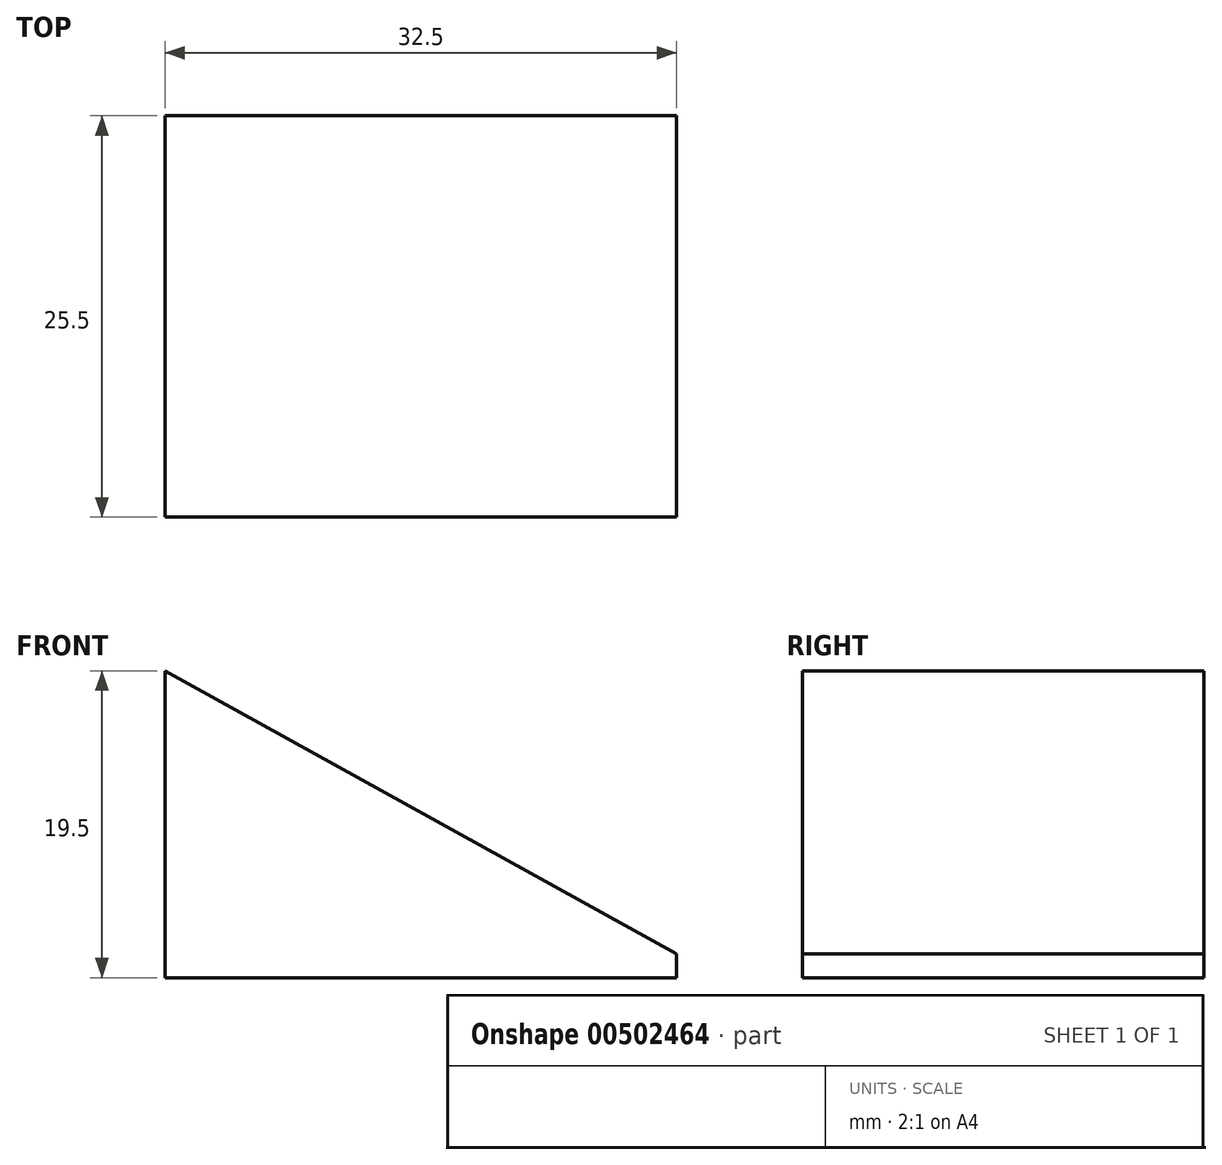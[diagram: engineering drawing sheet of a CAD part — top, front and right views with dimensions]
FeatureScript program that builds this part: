
annotation { "Feature Type Name" : "Feature", "Feature Type Description" : "" }
export const myFeature = defineFeature(function(context is Context, id is Id, definition is map)
    precondition{}
    {
        {
            var Q0;
            Q0=qCreatedBy(makeId("Top.planeOp"),FACE);
            var sketch = newSketch(context, id + "F0", { "sketchPlane" : qUnion([Q0])});
            skLineSegment(sketch, "E0.bottom", {"start": v(16.25, 12.75) * mm, "end": v(-16.25, 12.75) * mm});
            skLineSegment(sketch, "E0.top", {"start": v(16.25, -12.75) * mm, "end": v(-16.25, -12.75) * mm});
            skLineSegment(sketch, "E0.left", {"start": v(16.25, 12.75) * mm, "end": v(16.25, -12.75) * mm});
            skLineSegment(sketch, "E0.right", {"start": v(-16.25, 12.75) * mm, "end": v(-16.25, -12.75) * mm});
            skPoint(sketch, "E0.middle", {"position": v(0, 0) * mm});
            skSolve(sketch);
        }
        {
            var Q0;
            Q0=qCreatedBy(makeId("Front.planeOp"),FACE);
            cPlane(context, id + "F1", {"entities" : qUnion([Q0]), "cplaneType" : CPlaneType.OFFSET, "offset" : 12.75 * mm, "width" : 150 * mm, "height" : 150 * mm});
        }
        {
            var Q0;
            Q0=qCreatedBy(id+"F1.planeOp",FACE);
            var sketch = newSketch(context, id + "F2", { "sketchPlane" : qUnion([Q0])});
            skLineSegment(sketch, "E1.0", {"start": v(16.25, 0) * mm, "end": v(-16.25, 0) * mm});
            skLineSegment(sketch, "E2", {"start": v(-16.25, 0) * mm, "end": v(-16.25, 19.5) * mm});
            skLineSegment(sketch, "E3", {"start": v(16.25, 0) * mm, "end": v(16.25, 1.5) * mm});
            skLineSegment(sketch, "E4", {"start": v(16.25, 1.5) * mm, "end": v(-16.25, 19.5) * mm});
            skSolve(sketch);
        }
        {
            var Q0;
            Q0=makeQuery(id+"F2.imprint","IMPRINT",FACE,{"disambiguationData":[TD([[makeQuery(id+"F2.imprint","IMPRINT",EDGE,{"derivedFrom":sQuery(id+"F2.wireOp",EDGE,"E1.0")}),-1.0]])]});
            extrude(context, id + "F3", {"entities" : qUnion([Q0]), "oppositeDirection" : true, "depth" : 25.5 * mm});
        }
    });
